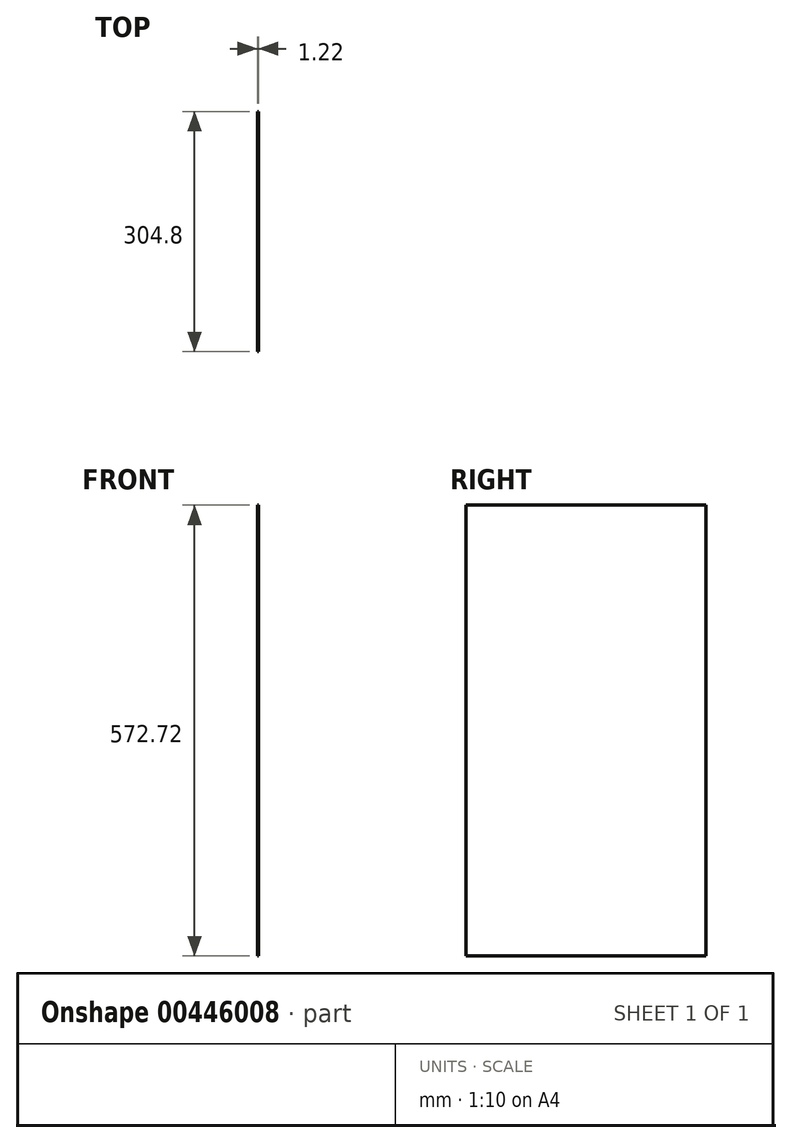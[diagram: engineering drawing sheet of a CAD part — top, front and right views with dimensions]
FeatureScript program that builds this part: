
annotation { "Feature Type Name" : "Feature", "Feature Type Description" : "" }
export const myFeature = defineFeature(function(context is Context, id is Id, definition is map)
    precondition{}
    {
        {
            var Q0;
            Q0=qCreatedBy(makeId("Front.planeOp"),FACE);
            var sketch = newSketch(context, id + "F0", { "sketchPlane" : qUnion([Q0])});
            skLineSegment(sketch, "E0.bottom", {"start": v(0.6, 286.36) * mm, "end": v(-0.6, 286.36) * mm});
            skLineSegment(sketch, "E0.top", {"start": v(0.6, -286.36) * mm, "end": v(-0.6, -286.36) * mm});
            skLineSegment(sketch, "E0.left", {"start": v(0.6, 286.36) * mm, "end": v(0.6, -286.36) * mm});
            skLineSegment(sketch, "E0.right", {"start": v(-0.6, 286.36) * mm, "end": v(-0.6, -286.36) * mm});
            skPoint(sketch, "E0.middle", {"position": v(0, 0) * mm});
            skSolve(sketch);
        }
        {
            var Q0;
            Q0 = qSketchRegion(id + "F0", true);
            extrude(context, id + "F1", {"entities" : qUnion([Q0]), "oppositeDirection" : true, "depth" : 304.8 * mm, "offsetDistance" : 25.4 * mm});
        }
    });
